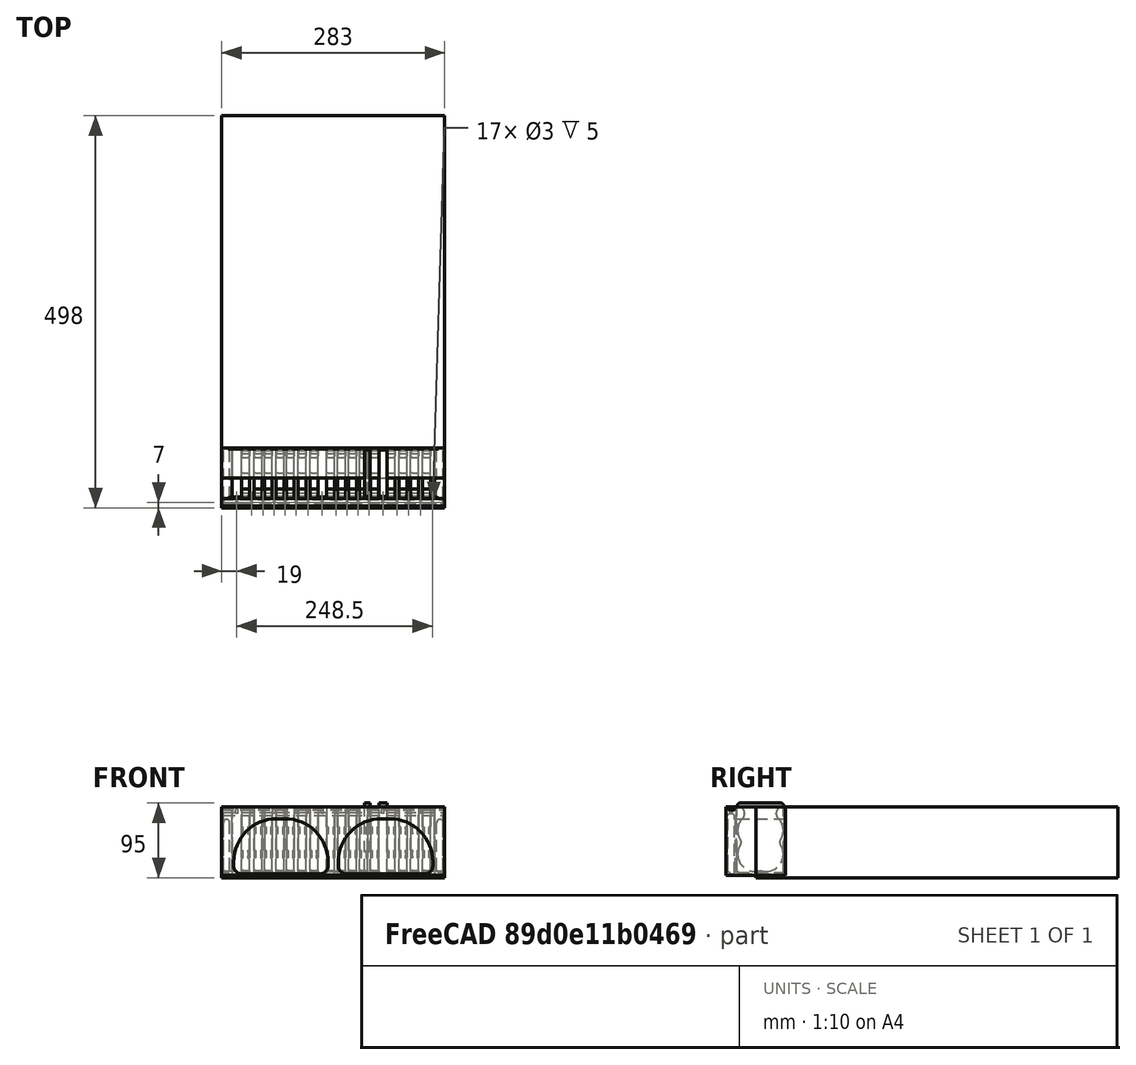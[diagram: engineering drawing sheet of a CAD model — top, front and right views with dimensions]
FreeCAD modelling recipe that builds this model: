
FCSTD DOCUMENT  (FreeCAD 0.16R6706 (Git))
Label: Dominion_Card_Tray_v0.1
License: All rights reserved
LicenseURL: http://en.wikipedia.org/wiki/All_rights_reserved
objects: Part::Box×28, Part::Cylinder×25, Part::Fillet×24, Part::MultiFuse×14, Part::Part2DObjectPython×2, Part::Extrusion×2, Part::Cut×2, Part::Chamfer×1
note: 98 computed .brp shape members not serialized (recipe doc carries the construction recipe); baked Part::Feature solids carry a one-line shape summary decoded from their .brp

FEATURE [Part::Box] Box  label="Curse_Cube"
  Height = 90
  Length = 7
  Placement = pos=(-3.5,-29.5,0) rot=(0,0,1;0rad)
  Width = 59
FEATURE [Part::Fillet] Fillet  label="20_Deck"
  Base = -> Box
  Edges = 4 edges r=4: [Edge9,Edge10,Edge11,Edge12]
  Placement = pos=(185,6,5) rot=(0,0,1;0rad)
FEATURE [Part::Box] Box001  label="Curse_Cube001"
  Height = 90
  Length = 4
  Placement = pos=(-2,-30.5,0) rot=(0,0,1;0rad)
  Width = 61
FEATURE [Part::Fillet] Fillet001  label="10_Curse_Deck_Hole_001"
  Base = -> Box001
  Edges = 4 edges r=4: [Edge9,Edge10,Edge11,Edge12]
  Placement = pos=(14,6,5) rot=(0,0,1;0rad)
FEATURE [Part::Box] Box002  label="Dominion_Box_Hole"
  Height = 90
  Length = 283
  Width = 460
FEATURE [Part::Box] Box003  label="Dominion_Box_Row"
  Height = 87
  Length = 283
  Placement = pos=(0,-38,3) rot=(0,0,1;0rad)
  Width = 76
FEATURE [Part::Box] Box004  label="Curse_Cube002"
  Height = 90
  Length = 10
  Placement = pos=(-5,-29.5,0) rot=(0,0,1;0rad)
  Width = 59
FEATURE [Part::Fillet] Fillet002  label="30_Deck"
  Base = -> Box004
  Edges = 4 edges r=4: [Edge9,Edge10,Edge11,Edge12]
  Placement = pos=(205,6,5) rot=(0,0,1;0rad)
FEATURE [Part::Box] Box005  label="Curse_Cube003"
  Height = 90
  Length = 11
  Placement = pos=(-5.5,-30.5,0) rot=(0,0,1;0rad)
  Width = 61
FEATURE [Part::Fillet] Fillet003  label="30_Curse_Deck_Hole"
  Base = -> Box005
  Edges = 4 edges r=4: [Edge9,Edge10,Edge11,Edge12]
  Placement = pos=(31.5,6,5) rot=(0,0,1;0rad)
FEATURE [Part::Box] Box006  label="LED_Channel"
  Height = 2.746
  Length = 283
  Placement = pos=(0,-34.847,86.464) rot=(0,0,1;0rad)
  Width = 7.694
FEATURE [Part::Cylinder] Cylinder001  label="30_Curse_LED_Hole"
  Angle = 360
  Height = 5
  Placement = pos=(31.5,-31,82) rot=(0,0,1;0rad)
  Radius = 1.5
FEATURE [Part::Cylinder] Cylinder002  label="10_Curse_LED_Hole_001"
  Angle = 360
  Height = 5
  Placement = pos=(14,-31,82) rot=(0,0,1;0rad)
  Radius = 1.5
FEATURE [Part::Box] Box008  label="Cube"
  Height = 20
  Length = 257
  Placement = pos=(0,-13,70) rot=(0,0,1;0rad)
  Width = 40
FEATURE [Part::Box] Box007  label="Hole_For_Wiring001"
  Height = 78
  Length = 279
  Placement = pos=(2,-36,5) rot=(0,0,1;0rad)
  Width = 9
FEATURE [Part::Box] Box009  label="Curse_Cube004"
  Height = 90
  Length = 4
  Placement = pos=(-2,-30.5,0) rot=(0,0,1;0rad)
  Width = 61
FEATURE [Part::Fillet] Fillet004  label="10_Curse_Deck_Hole_002"
  Base = -> Box009
  Edges = 4 edges r=4: [Edge9,Edge10,Edge11,Edge12]
  Placement = pos=(0,6,5) rot=(0,0,1;0rad)
FEATURE [Part::Cylinder] Cylinder004  label="10_Curse_LED_Hole_002"
  Angle = 360
  Height = 5
  Placement = pos=(0,-31,82) rot=(0,0,1;0rad)
  Radius = 1.5
FEATURE [Part::Box] Box011  label="Curse_Cube006"
  Height = 90
  Length = 4
  Placement = pos=(-2,-30.5,0) rot=(0,0,1;0rad)
  Width = 61
FEATURE [Part::Fillet] Fillet006  label="9_Gold_Deck_Hole_001"
  Base = -> Box011
  Edges = 4 edges r=4: [Edge9,Edge10,Edge11,Edge12]
  Placement = pos=(31.5,6,5) rot=(0,0,1;0rad)
FEATURE [Part::Box] Box012  label="Curse_Cube007"
  Height = 90
  Length = 4
  Placement = pos=(-2,-30.5,0) rot=(0,0,1;0rad)
  Width = 61
FEATURE [Part::Fillet] Fillet007  label="9_Gold_Deck_Hole_002"
  Base = -> Box012
  Edges = 4 edges r=4: [Edge9,Edge10,Edge11,Edge12]
  Placement = pos=(17.5,6,5) rot=(0,0,1;0rad)
FEATURE [Part::Box] Box013  label="Curse_Cube008"
  Height = 90
  Length = 11
  Placement = pos=(-5.5,-30.5,0) rot=(0,0,1;0rad)
  Width = 61
FEATURE [Part::Fillet] Fillet008  label="30_Gold_Deck_Hole"
  Base = -> Box013
  Edges = 4 edges r=4: [Edge9,Edge10,Edge11,Edge12]
  Placement = pos=(0,6,5) rot=(0,0,1;0rad)
FEATURE [Part::MultiFuse] Fusion  label="Curse_Holes"
  Placement = pos=(176,0,0) rot=(0,0,1;0rad)
  Shapes = -> [Fillet003,Cylinder004,Cylinder001,Cylinder002,Fillet001,Fillet004]
FEATURE [Part::Cylinder] Cylinder005  label="9_Gold_LED_Hole_001"
  Angle = 360
  Height = 5
  Placement = pos=(31.5,-31,82) rot=(0,0,1;0rad)
  Radius = 1.5
FEATURE [Part::Cylinder] Cylinder006  label="30_Gold_LED_Hole"
  Angle = 360
  Height = 5
  Placement = pos=(0,-31,82) rot=(0,0,1;0rad)
  Radius = 1.5
FEATURE [Part::Cylinder] Cylinder007  label="9_Gold_LED_Hole"
  Angle = 360
  Height = 5
  Placement = pos=(17.5,-31,82) rot=(0,0,1;0rad)
  Radius = 1.5
FEATURE [Part::MultiFuse] Fusion003  label="Gold_Holes"
  Placement = pos=(130.5,0,0) rot=(0,0,1;0rad)
  Shapes = -> [Fillet008,Fillet006,Fillet007,Cylinder005,Cylinder006,Cylinder007]
FEATURE [Part::Box] Box016  label="Curse_Cube011"
  Height = 90
  Length = 5
  Placement = pos=(-2.5,-30.5,0) rot=(0,0,1;0rad)
  Width = 61
FEATURE [Part::Fillet] Fillet012  label="12_Platinum_Deck_Hole"
  Base = -> Box016
  Edges = 4 edges r=4: [Edge9,Edge10,Edge11,Edge12]
  Placement = pos=(0,6,5) rot=(0,0,1;0rad)
FEATURE [Part::Cylinder] Cylinder008  label="12_Platinum_LED_Hole"
  Angle = 360
  Height = 5
  Placement = pos=(0,-31,82) rot=(0,0,1;0rad)
  Radius = 1.5
FEATURE [Part::MultiFuse] Fusion004  label="Platinum_Holes"
  Placement = pos=(112.5,0,0) rot=(0,0,1;0rad)
  Shapes = -> [Fillet012,Cylinder008]
FEATURE [Part::Box] Box017  label="Cube012"
  Height = 90
  Length = 5
  Placement = pos=(-2.5,-30.5,0) rot=(0,0,1;0rad)
  Width = 61
FEATURE [Part::Fillet] Fillet013  label="12_Provience_Deck_Hole"
  Base = -> Box017
  Edges = 4 edges r=4: [Edge9,Edge10,Edge11,Edge12]
  Placement = pos=(14,6,5) rot=(0,0,1;0rad)
FEATURE [Part::Cylinder] Cylinder009  label="12_Provience_LED_Hole"
  Angle = 360
  Height = 5
  Placement = pos=(14,-31,82) rot=(0,0,1;0rad)
  Radius = 1.5
FEATURE [Part::Box] Box018  label="Cube013"
  Height = 90
  Length = 3
  Placement = pos=(-1.5,-30.5,0) rot=(0,0,1;0rad)
  Width = 61
FEATURE [Part::Fillet] Fillet014  label="6_Provience_Deck_Hole"
  Base = -> Box018
  Edges = 4 edges r=4: [Edge9,Edge10,Edge11,Edge12]
  Placement = pos=(0,6,5) rot=(0,0,1;0rad)
FEATURE [Part::Cylinder] Cylinder010  label="6_Provience_LED_Hole"
  Angle = 360
  Height = 5
  Placement = pos=(0,-31,82) rot=(0,0,1;0rad)
  Radius = 1.5
FEATURE [Part::MultiFuse] Fusion005  label="Provience_Holes"
  Placement = pos=(83.5,0,0) rot=(0,0,1;0rad)
  Shapes = -> [Fillet013,Cylinder009,Fillet014,Cylinder010]
FEATURE [Part::Box] Box019  label="Curse_Cube012"
  Height = 90
  Length = 5
  Placement = pos=(-2.5,-30.5,0) rot=(0,0,1;0rad)
  Width = 61
FEATURE [Part::Fillet] Fillet015  label="12_Dutchy_Deck_Hole"
  Base = -> Box019
  Edges = 4 edges r=4: [Edge9,Edge10,Edge11,Edge12]
  Placement = pos=(0,6,5) rot=(0,0,1;0rad)
FEATURE [Part::Cylinder] Cylinder011  label="12_Dutchy_LED_Hole"
  Angle = 360
  Height = 5
  Placement = pos=(0,-31,82) rot=(0,0,1;0rad)
  Radius = 1.5
FEATURE [Part::MultiFuse] Fusion006  label="Dutchy_Holes"
  Placement = pos=(69.5,0,0) rot=(0,0,1;0rad)
  Shapes = -> [Fillet015,Cylinder011]
FEATURE [Part::Box] Box020  label="Cube014"
  Height = 90
  Length = 6
  Placement = pos=(-3,-30.5,0) rot=(0,0,1;0rad)
  Width = 61
FEATURE [Part::Fillet] Fillet016  label="24_Estate_Deck_Hole"
  Base = -> Box020
  Edges = 4 edges r=4: [Edge9,Edge10,Edge11,Edge12]
  Placement = pos=(0,6,5) rot=(0,0,1;0rad)
FEATURE [Part::Cylinder] Cylinder012  label="24_Estate_LED_Hole"
  Angle = 360
  Height = 5
  Placement = pos=(0,-31,82) rot=(0,0,1;0rad)
  Radius = 1.5
FEATURE [Part::Box] Box021  label="Cube015"
  Height = 90
  Length = 3
  Placement = pos=(-1.5,-30.5,0) rot=(0,0,1;0rad)
  Width = 61
FEATURE [Part::Fillet] Fillet017  label="6_Estate_Deck_Hole"
  Base = -> Box021
  Edges = 4 edges r=4: [Edge9,Edge10,Edge11,Edge12]
  Placement = pos=(14.5,6,5) rot=(0,0,1;0rad)
FEATURE [Part::Cylinder] Cylinder013  label="6_Estate_LED_Hole"
  Angle = 360
  Height = 5
  Placement = pos=(14.5,-31,82) rot=(0,0,1;0rad)
  Radius = 1.5
FEATURE [Part::MultiFuse] Fusion007  label="Estate_Holes"
  Placement = pos=(41,0,0) rot=(0,0,1;0rad)
  Shapes = -> [Fillet016,Cylinder012,Fillet017,Cylinder013]
FEATURE [Part::Box] Box022  label="Curse_Cube013"
  Height = 90
  Length = 12
  Placement = pos=(-6,-30.5,0) rot=(0,0,1;0rad)
  Width = 61
FEATURE [Part::Fillet] Fillet018  label="30_Silver_Deck_Hole"
  Base = -> Box022
  Edges = 4 edges r=4: [Edge9,Edge10,Edge11,Edge12]
  Placement = pos=(0,6,5) rot=(0,0,1;0rad)
FEATURE [Part::Cylinder] Cylinder014  label="30_Silver_LED_Hole"
  Angle = 360
  Height = 5
  Placement = pos=(0,-31,82) rot=(0,0,1;0rad)
  Radius = 1.5
FEATURE [Part::MultiFuse] Fusion008  label="Silver_Holes"
  Placement = pos=(22,0,0) rot=(0,0,1;0rad)
  Shapes = -> [Fillet018,Cylinder014]
FEATURE [Part::Box] Box023  label="Curse_Cube014"
  Height = 90
  Length = 5
  Placement = pos=(-2.5,-30.5,0) rot=(0,0,1;0rad)
  Width = 61
FEATURE [Part::Fillet] Fillet019  label="12_Extra_Deck_Hole001"
  Base = -> Box023
  Edges = 4 edges r=4: [Edge9,Edge10,Edge11,Edge12]
  Placement = pos=(0,6,5) rot=(0,0,1;0rad)
FEATURE [Part::Cylinder] Cylinder015  label="12_Extra_LED_Hole001"
  Angle = 360
  Height = 5
  Placement = pos=(0,-31,82) rot=(0,0,1;0rad)
  Radius = 1.5
FEATURE [Part::Box] Box024  label="Curse_Cube015"
  Height = 90
  Length = 5
  Placement = pos=(-2.5,-30.5,0) rot=(0,0,1;0rad)
  Width = 61
FEATURE [Part::Fillet] Fillet020  label="12_Extra_Deck_Hole002"
  Base = -> Box024
  Edges = 4 edges r=4: [Edge9,Edge10,Edge11,Edge12]
  Placement = pos=(15,6,5) rot=(0,0,1;0rad)
FEATURE [Part::Box] Box025  label="Curse_Cube016"
  Height = 90
  Length = 5
  Placement = pos=(-2.5,-30.5,0) rot=(0,0,1;0rad)
  Width = 61
FEATURE [Part::Fillet] Fillet021  label="12_Extra_Deck_Hole003"
  Base = -> Box025
  Edges = 4 edges r=4: [Edge9,Edge10,Edge11,Edge12]
  Placement = pos=(30,6,5) rot=(0,0,1;0rad)
FEATURE [Part::Box] Box026  label="Curse_Cube017"
  Height = 90
  Length = 5
  Placement = pos=(-2.5,-30.5,0) rot=(0,0,1;0rad)
  Width = 61
FEATURE [Part::Fillet] Fillet022  label="12_Extra_Deck_Hole004"
  Base = -> Box026
  Edges = 4 edges r=4: [Edge9,Edge10,Edge11,Edge12]
  Placement = pos=(45,6,5) rot=(0,0,1;0rad)
FEATURE [Part::Cylinder] Cylinder016  label="12_Extra_LED_Hole002"
  Angle = 360
  Height = 5
  Placement = pos=(15,-31,82) rot=(0,0,1;0rad)
  Radius = 1.5
FEATURE [Part::Cylinder] Cylinder017  label="12_Extra_LED_Hole003"
  Angle = 360
  Height = 5
  Placement = pos=(30,-31,82) rot=(0,0,1;0rad)
  Radius = 1.5
FEATURE [Part::Cylinder] Cylinder018  label="12_Extra_LED_Hole004"
  Angle = 360
  Height = 5
  Placement = pos=(45,-31,82) rot=(0,0,1;0rad)
  Radius = 1.5
FEATURE [Part::MultiFuse] Fusion009  label="Extra_Holes"
  Placement = pos=(225.5,0,0) rot=(0,0,1;0rad)
  Shapes = -> [Fillet019,Cylinder015,Fillet020,Fillet021,Fillet022,Cylinder016,Cylinder017,Cylinder018]
FEATURE [Part::MultiFuse] Fusion010  label="Holes"
  Placement = pos=(-3,0,0) rot=(0,0,1;0rad)
  Shapes = -> [Fusion004,Fusion005,Fusion008,Fusion003,Fusion,Fusion009,Fusion007,Fusion006]
FEATURE [Part::Cylinder] Cylinder019
  Angle = 360
  Height = 257
  Placement = pos=(0,14,60) rot=(0,1,0;1.5708rad)
  Radius = 22
FEATURE [Part::Cylinder] Cylinder020
  Angle = 360
  Height = 257
  Placement = pos=(0,0,60) rot=(0,1,0;1.5708rad)
  Radius = 22
FEATURE [Part::Part2DObjectPython] DWire  # Draft 2D object (typed FeaturePython)
  ChamferSize = 0
  Closed = true
  End = (0,-4.845,3.563)
  FilletRadius = 0
  Length = 31.331
  MakeFace = true
  Points = (16) [(0,4.845,3.563),(0,4.845,2.939),(0,4.138,2.315),(0,4.138,0.9),(0,4.554,0.5262),(0,3.847,0),(0,3.514,0.333),(0,3.514,2.746),(0,-3.514,2.746),+7 more]
  Start = (0,4.845,3.563)
  Subdivisions = 0
FEATURE [Part::Extrusion] Extrude  label="LED_Diffuser"
  Base = -> DWire
  Dir = (283,0,0)
  Placement = pos=(0,-31,86.464) rot=(0,0,1;0rad)
  Solid = true
FEATURE [Part::Part2DObjectPython] DWire001  # Draft 2D object (typed FeaturePython)
  ChamferSize = 0
  Closed = true
  End = (0,-4.845,3.563)
  FilletRadius = 0
  Length = 31.331
  MakeFace = true
  Points = (16) [(0,4.845,3.563),(0,4.845,2.939),(0,4.138,2.315),(0,4.138,0.9),(0,4.554,0.5262),(0,3.847,0),(0,3.514,0.333),(0,3.514,2.746),(0,-3.514,2.746),+7 more]
  Start = (0,4.845,3.563)
  Subdivisions = 0
FEATURE [Part::Extrusion] Extrude001  label="LED_Diffuser_Hole"
  Base = -> DWire001
  Dir = (283,0,0)
  Placement = pos=(0,-31,86.464) rot=(0,0,1;0rad)
  Solid = true
FEATURE [Part::MultiFuse] Fusion012  label="LED_Cut"
  Shapes = -> [Extrude001,Box006]
FEATURE [Part::Box] Box027  label="Hole_For_Wiring002"
  Height = 70
  Length = 120
  Placement = pos=(15,-38,5) rot=(0,0,1;0rad)
  Width = 10
FEATURE [Part::Fillet] Fillet025
  Base = -> Box027
  Edges = 4 edges: [Edge2 r=55,Edge4 r=10,Edge6 r=55,Edge8 r=10]
FEATURE [Part::Box] Box028  label="Hole_For_Wiring003"
  Height = 70
  Length = 120
  Placement = pos=(148,-38,5) rot=(0,0,1;0rad)
  Width = 10
FEATURE [Part::Fillet] Fillet026
  Base = -> Box028
  Edges = 4 edges: [Edge2 r=55,Edge4 r=10,Edge6 r=55,Edge8 r=10]
FEATURE [Part::Cylinder] Cylinder
  Angle = 360
  Height = 64
  Placement = pos=(6,38,10) rot=(1,0,0;1.5708rad)
  Radius = 4
FEATURE [Part::Cylinder] Cylinder021
  Angle = 360
  Height = 64
  Placement = pos=(6,38,70) rot=(1,0,0;1.5708rad)
  Radius = 4
FEATURE [Part::Box] Box029  label="Cube016"
  Height = 60
  Length = 8
  Placement = pos=(2,-26,10) rot=(0,0,1;0rad)
  Width = 64
FEATURE [Part::MultiFuse] Fusion013
  Shapes = -> [Cylinder,Cylinder021,Box029]
FEATURE [Part::Cylinder] Cylinder022
  Angle = 360
  Height = 64
  Placement = pos=(4,38,10) rot=(1,0,0;1.5708rad)
  Radius = 4
FEATURE [Part::Cylinder] Cylinder023
  Angle = 360
  Height = 64
  Placement = pos=(4,38,70) rot=(1,0,0;1.5708rad)
  Radius = 4
FEATURE [Part::Box] Box030  label="Cube017"
  Height = 60
  Length = 8
  Placement = pos=(0,-26,10) rot=(0,0,1;0rad)
  Width = 64
FEATURE [Part::MultiFuse] Fusion014
  Placement = pos=(273,0,0) rot=(0,0,1;0rad)
  Shapes = -> [Cylinder022,Cylinder023,Box030]
FEATURE [Part::Chamfer] Chamfer
  Base = -> Box007
  Edges = 3 edges r=4: [Edge9,Edge10,Edge12]
FEATURE [Part::MultiFuse] Fusion015
  Shapes = -> [Chamfer,Fillet025,Fillet026,Fusion013,Fusion014]
FEATURE [Part::Cylinder] Cylinder024
  Angle = 360
  Height = 257
  Placement = pos=(0,0,30) rot=(0,1,0;1.5708rad)
  Radius = 22
FEATURE [Part::Cylinder] Cylinder025
  Angle = 360
  Height = 257
  Placement = pos=(0,14,30) rot=(0,1,0;1.5708rad)
  Radius = 22
FEATURE [Part::MultiFuse] Fusion016
  Placement = pos=(13,-1,0) rot=(0,0,1;0rad)
  Shapes = -> [Cylinder019,Cylinder020,Cylinder024,Cylinder025,Box008]
FEATURE [Part::Cut] Cut
  Base = -> Box003
  Tool = -> Fusion016
FEATURE [Part::Fillet] Fillet027
  Base = -> Cut
  Edges = 6 edges r=8: [Edge10,Edge12,Edge18,Edge24,Edge29,Edge38]
FEATURE [Part::Cut] Cut001
  Base = -> Fillet027
  Tool = -> Fusion010
FEATURE [Part::Fillet] Fillet028
  Base = -> Cut001
  Edges = 64 edges r=2: [Edge183,Edge186,Edge203,Edge206,Edge223,Edge226,Edge243,Edge246,Edge263,Edge266,Edge283,Edge286,Edge303,Edge306,Edge323,Edge326,Edge343,Edge346,Edge363,Edge366,Edge383,Edge386,Edge403,Edge406,Edge423,Edge426,Edge443,Edge446,Edge463,Edge466,Edge483,Edge486,Edge503,Edge506,Edge523,Edge526,Edge543,+27 more]
FEATURE [Part::Fillet] Fillet029
  Base = -> Fillet028
  Edges = 4 edges: [Edge6 r=1,Edge12 r=5,Edge187 r=1,Edge193 r=5]
